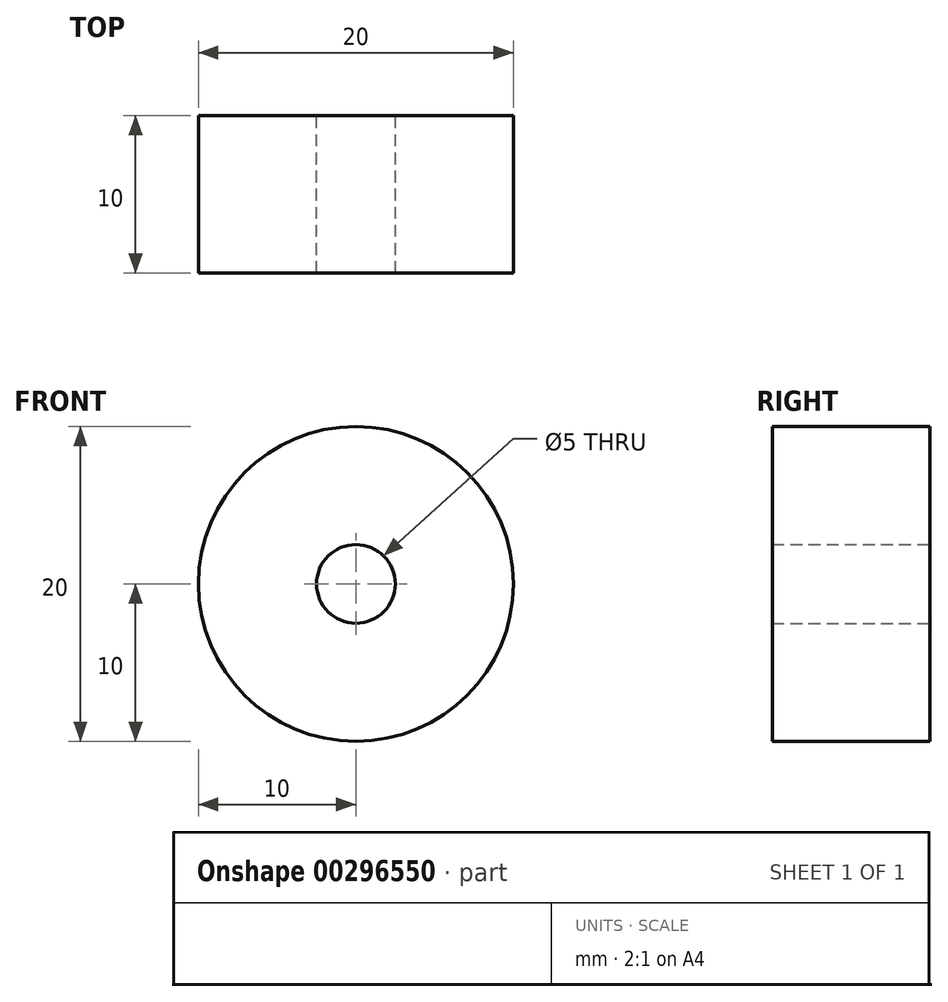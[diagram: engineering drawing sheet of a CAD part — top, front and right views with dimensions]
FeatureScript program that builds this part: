
annotation { "Feature Type Name" : "Feature", "Feature Type Description" : "" }
export const myFeature = defineFeature(function(context is Context, id is Id, definition is map)
    precondition{}
    {
        {
            var Q0;
            Q0=qCreatedBy(makeId("Front.planeOp"),FACE);
            var sketch = newSketch(context, id + "F0", { "sketchPlane" : qUnion([Q0])});
            skCircle(sketch, "E0", {"center": v(0, 0) * mm, "radius": 10 * mm});
            skCircle(sketch, "E1", {"center": v(0, 0) * mm, "radius": 2.5 * mm});
            skSolve(sketch);
        }
        {
            var Q0;
            Q0 = qSketchRegion(id + "F0", true);
            extrude(context, id + "F1", {"entities" : qUnion([Q0]), "depth" : 10 * mm, "symmetric" : true});
        }
    });
